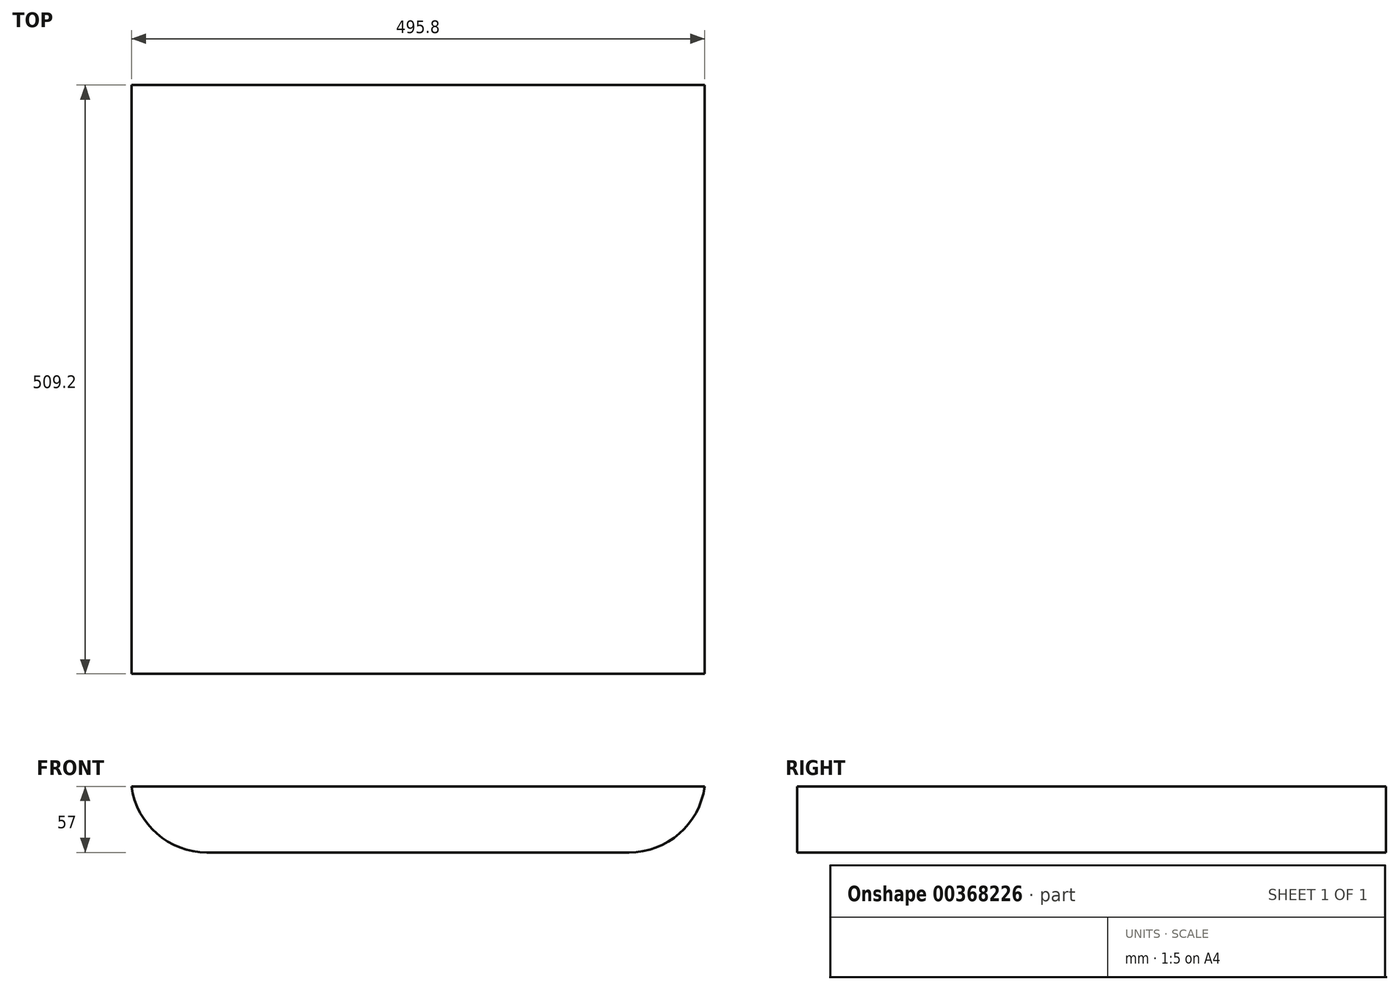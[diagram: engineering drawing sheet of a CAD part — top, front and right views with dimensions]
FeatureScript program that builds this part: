
annotation { "Feature Type Name" : "Feature", "Feature Type Description" : "" }
export const myFeature = defineFeature(function(context is Context, id is Id, definition is map)
    precondition{}
    {
        {
            var Q0;
            Q0=qCreatedBy(makeId("Top.planeOp"),FACE);
            var sketch = newSketch(context, id + "F0", { "sketchPlane" : qUnion([Q0])});
            skLineSegment(sketch, "E0.bottom", {"start": v(0, 0) * mm, "end": v(495.8, 0) * mm});
            skLineSegment(sketch, "E0.top", {"start": v(0, -509.2) * mm, "end": v(495.8, -509.2) * mm});
            skLineSegment(sketch, "E0.left", {"start": v(0, 0) * mm, "end": v(0, -509.2) * mm});
            skLineSegment(sketch, "E0.right", {"start": v(495.8, 0) * mm, "end": v(495.8, -509.2) * mm});
            skSolve(sketch);
        }
        {
            var Q0;
            Q0 = qSketchRegion(id + "F0", true);
            extrude(context, id + "F1", {"entities" : qUnion([Q0]), "depth" : 57 * mm, "offsetDistance" : 25 * mm});
        }
        {
            var Q0;
            Q0=makeQuery(id+"F1.opExtrude","CAP_EDGE",EDGE,{"disambiguationData":[OSD([sQuery(id+"F0.wireOp",EDGE,"E0.left")])],"isStart":true});
            var Q1;
            Q1=makeQuery(id+"F1.opExtrude","CAP_EDGE",EDGE,{"disambiguationData":[OSD([sQuery(id+"F0.wireOp",EDGE,"E0.right")])],"isStart":true});
            fillet(context, id + "F2", {"entities" : qUnion([Q0, Q1]), "radius" : 66 * mm, "tangentPropagation" : true, "allowEdgeOverflow" : false});
        }
    });
